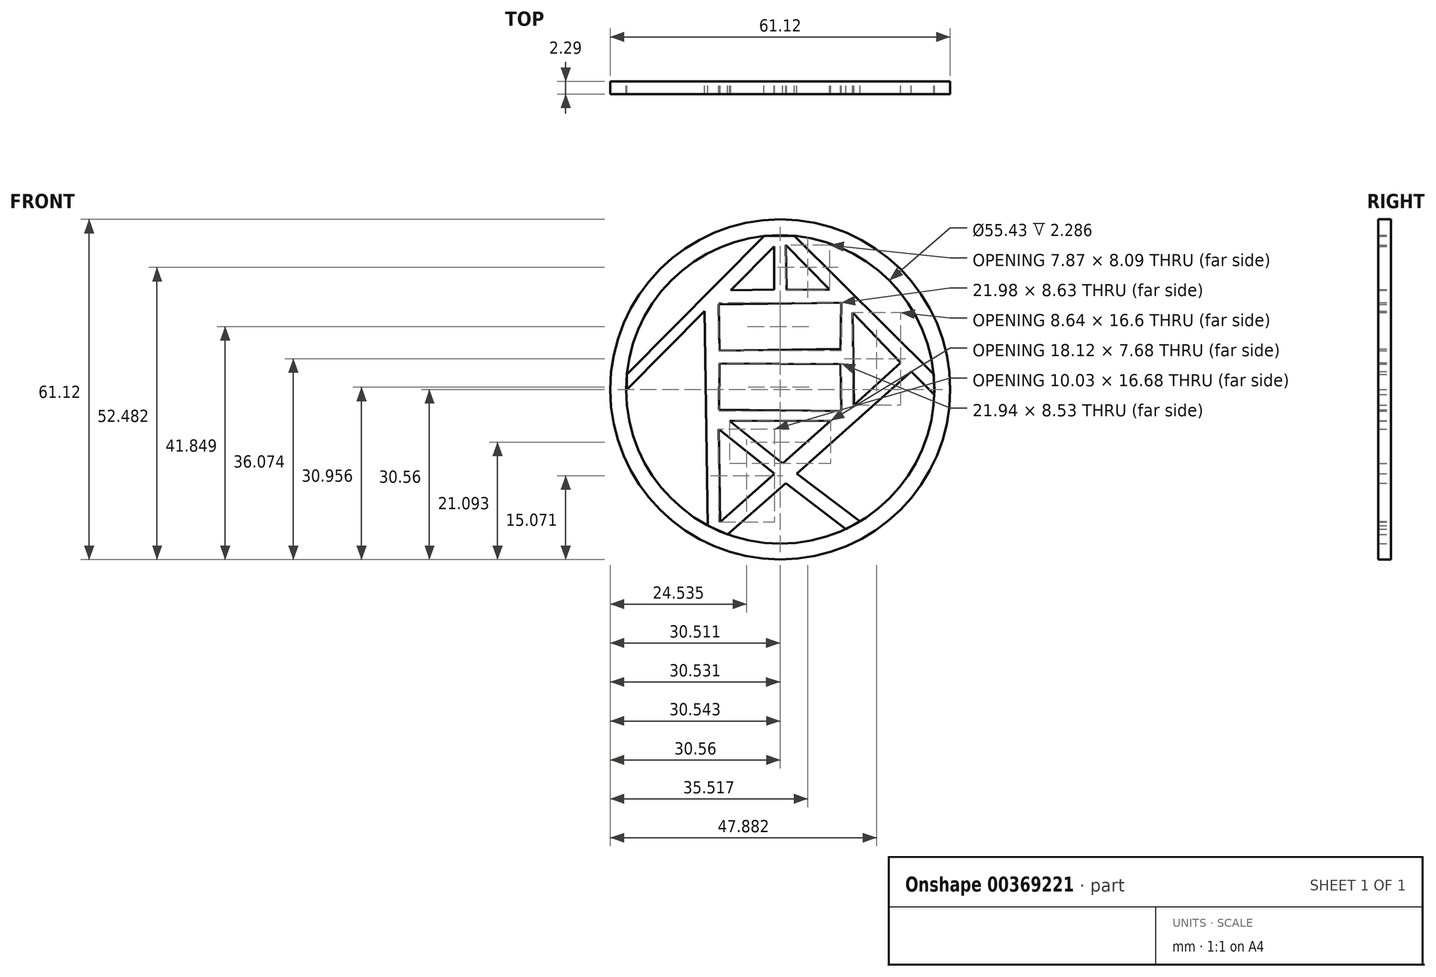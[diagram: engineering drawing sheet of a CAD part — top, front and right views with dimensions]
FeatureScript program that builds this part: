
annotation { "Feature Type Name" : "Feature", "Feature Type Description" : "" }
export const myFeature = defineFeature(function(context is Context, id is Id, definition is map)
    precondition{}
    {
        {
            var Q0;
            Q0=qCreatedBy(makeId("Front.planeOp"),FACE);
            var sketch = newSketch(context, id + "F0", { "sketchPlane" : qUnion([Q0])});
            skCircle(sketch, "E0", {"center": v(0, 0) * mm, "radius": 30.56 * mm});
            skCircle(sketch, "E1", {"center": v(0, 0) * mm, "radius": 27.71 * mm});
            skLineSegment(sketch, "E2", {"start": v(-2.92, 27.56) * mm, "end": v(-27.58, 2.72) * mm});
            skLineSegment(sketch, "E3", {"start": v(-27.58, 2.72) * mm, "end": v(-27.58, 0) * mm});
            skLineSegment(sketch, "E4", {"start": v(-27.58, 0) * mm, "end": v(-13.61, 14.07) * mm});
            skLineSegment(sketch, "E5", {"start": v(-13.61, 14.07) * mm, "end": v(-13.03, -24.46) * mm});
            skLineSegment(sketch, "E6", {"start": v(-13.03, -24.46) * mm, "end": v(-9.46, -26.05) * mm});
            skLineSegment(sketch, "E7", {"start": v(-9.46, -26.05) * mm, "end": v(1.02, -16.82) * mm});
            skLineSegment(sketch, "E8", {"start": v(1.02, -16.82) * mm, "end": v(11.79, -25.08) * mm});
            skLineSegment(sketch, "E9", {"start": v(11.79, -25.08) * mm, "end": v(14.36, -23.7) * mm});
            skLineSegment(sketch, "E10", {"start": v(14.36, -23.7) * mm, "end": v(3, -15.1) * mm});
            skLineSegment(sketch, "E11", {"start": v(3, -15.1) * mm, "end": v(23.53, 3.2) * mm});
            skLineSegment(sketch, "E12", {"start": v(23.53, 3.2) * mm, "end": v(27.7, -0.94) * mm});
            skLineSegment(sketch, "E13", {"start": v(27.7, -0.94) * mm, "end": v(27.58, 2.7) * mm});
            skLineSegment(sketch, "E14", {"start": v(27.58, 2.7) * mm, "end": v(2.5, 27.6) * mm});
            skLineSegment(sketch, "E15", {"start": v(2.5, 27.6) * mm, "end": v(-2.92, 27.56) * mm});
            skLineSegment(sketch, "E16", {"start": v(-8.9, 17.84) * mm, "end": v(-1.1, 25.7) * mm});
            skLineSegment(sketch, "E17", {"start": v(-1.1, 25.7) * mm, "end": v(-1.1, 17.92) * mm});
            skLineSegment(sketch, "E18", {"start": v(-1.1, 17.92) * mm, "end": v(-8.9, 17.84) * mm});
            skLineSegment(sketch, "E19", {"start": v(1.02, 25.97) * mm, "end": v(1.11, 17.88) * mm});
            skPoint(sketch, "E19.endSnap0", {"position": v(-5, 17.88) * mm});
            skLineSegment(sketch, "E20", {"start": v(1.11, 17.88) * mm, "end": v(8.9, 17.96) * mm});
            skLineSegment(sketch, "E21", {"start": v(8.9, 17.96) * mm, "end": v(1.02, 25.97) * mm});
            skLineSegment(sketch, "E22", {"start": v(-10.91, 6.97) * mm, "end": v(10.86, 7.3) * mm});
            skLineSegment(sketch, "E23", {"start": v(-10.91, 6.97) * mm, "end": v(-11.04, 15.27) * mm});
            skLineSegment(sketch, "E24", {"start": v(-11.04, 15.27) * mm, "end": v(10.94, 15.6) * mm});
            skLineSegment(sketch, "E25", {"start": v(10.94, 15.6) * mm, "end": v(10.86, 7.3) * mm});
            skLineSegment(sketch, "E26", {"start": v(13, 13.81) * mm, "end": v(13.25, -2.79) * mm});
            skLineSegment(sketch, "E27", {"start": v(13.25, -2.79) * mm, "end": v(21.64, 4.83) * mm});
            skLineSegment(sketch, "E28", {"start": v(21.64, 4.83) * mm, "end": v(13, 13.81) * mm});
            skLineSegment(sketch, "E29", {"start": v(-10.91, 4.66) * mm, "end": v(-11, -3.64) * mm});
            skLineSegment(sketch, "E30", {"start": v(-11, -3.64) * mm, "end": v(10.94, -3.87) * mm});
            skLineSegment(sketch, "E31", {"start": v(10.94, -3.87) * mm, "end": v(10.81, 4.58) * mm});
            skLineSegment(sketch, "E32", {"start": v(-9.07, -5.7) * mm, "end": v(0.42, -13.3) * mm});
            skLineSegment(sketch, "E33", {"start": v(0.42, -13.3) * mm, "end": v(9.04, -5.63) * mm});
            skLineSegment(sketch, "E34", {"start": v(9.04, -5.63) * mm, "end": v(-9.07, -5.7) * mm});
            skLineSegment(sketch, "E35", {"start": v(-11.04, -7.15) * mm, "end": v(-10.8, -23.83) * mm});
            skLineSegment(sketch, "E36", {"start": v(-10.8, -23.83) * mm, "end": v(-1, -15.1) * mm});
            skLineSegment(sketch, "E37", {"start": v(-1, -15.1) * mm, "end": v(-11.04, -7.15) * mm});
            skLineSegment(sketch, "E38", {"start": v(10.81, 4.58) * mm, "end": v(-10.91, 4.66) * mm});
            skSolve(sketch);
        }
        {
            var Q0;
            Q0 = qSketchRegion(id + "F0", true);
            var Q1;
            Q1=makeQuery(id+"F0.imprint","IMPRINT",FACE,{"disambiguationData":[TD([[makeQuery(id+"F0.imprint","IMPRINT",EDGE,{"derivedFrom":sQuery(id+"F0.wireOp",EDGE,"E2")}),1.0]])]});
            extrude(context, id + "F1", {"entities" : qUnion([Q0, Q1]), "depth" : 2.3 * mm});
        }
    });
